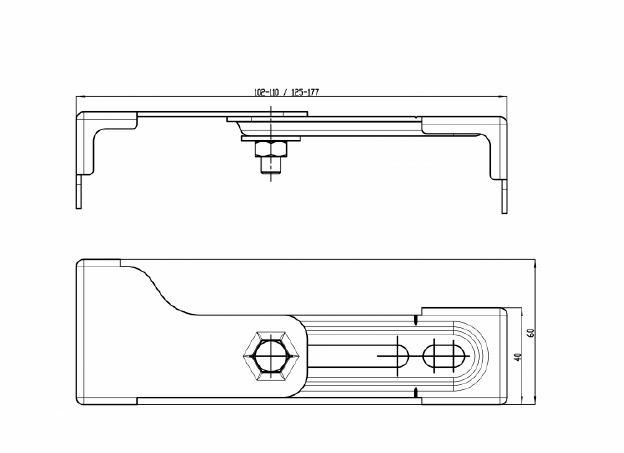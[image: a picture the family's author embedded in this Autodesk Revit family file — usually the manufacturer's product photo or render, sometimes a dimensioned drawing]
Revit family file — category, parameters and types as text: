
# Revit family: PRD_AR_PrplmbInstlFrm_InstallationFrameForUrinal_CMPX136,137
name_source: partatom
category: Plumbing Fixtures
revit_build: Autodesk Revit 2018 (Build: 20190510_1515(x64)
units: mm (PartAtom-declared; Revit-internal decimal feet)

## family parameters
Always vertical = Yes
Cut with Voids When Loaded = Yes
OmniClass Number = 23.40.20.00
OmniClass Title = General Furniture and Specialties
Part Type = Normal
Room Calculation Point = No
Round Connector Dimension = Use Diameter
Shared = Yes
Work Plane-Based = No

## types (2) — shared parameters
1stBeamOffset = 425 mm  [stored 1.39436 ft]
1stBeamOffsetVertical = 425 mm  [stored 1.39436 ft]
2ndBeamOffset = 815 mm  [stored 2.67388 ft]
2ndBeamOffsetVertical = 815 mm  [stored 2.67388 ft]
3rdBeamOffset = 975 mm
4thBeamVisibility = No
AssetType = Fixed
Category = Pr_40_20_93_62, Pre-plumbed installation frames
CisternCapacity = 0
CisternHeight = None
DiameterNominal = 15  [stored 0.0492126 ft]
DurationUnit = year
Features = steel, wall and floor mounting, 525x1120x135 mm (WxHxD)
Finish = powder coated
FlushRate = 0
FlushType = Unset
Form = Installation frame
FrameMaterial = PRD_AR_StainlessSteel_Colored
HeightAdjustment = 200 mm  [stored 0.656168 ft]
IfcExportAs = IfcSanitaryTerminalType
IfcExportType = CISTERN
InletSize = DN 15 (1/2 inch.)
IsAutomaticFlush = 0
IsSingleFlush = 0
Manufacturer = KWC Group AG
ManufacturerName = KWC Group AG
ManufacturerURL = www.kwc.com
Materials = powder coated steel
NBSDescription = Preplumbed installation frames
NBSReference = 45-35-70/421
NominalHeight = 1120 mm  [stored 3.67454 ft]
NominalLength = 135 mm
NominalWidth = 525 mm
OutletOffset = 100 mm  [stored 0.328084 ft]
OutletOffsetVertical = 100 mm  [stored 0.328084 ft]
OutletSize = DN 50 (2 inch.)
OverallHeight = 1120 mm  [stored 3.67454 ft]
PipeMaterial = PRD_AR_OutletPipe
ProductInformation = https://pim.kwc.com
Size = 525x1120x135 mm
SteelMaterial = PRD_AR_StainlessSteel_SatinFinished
URL = www.kwc.com
Uniclass2015Code = Pr_40_20_93_62
Uniclass2015Title = Pre-plumbed installation frames
Uniclass2015Version = Products v1.10
ValveVisibility = No
Version = 1
WarrantyDurationUnit = year
WasteSize = 50  [stored 0.164042 ft]

## per-type parameters (varying)
| type | 2ndBeamVisibility | BIMObjectName | Description | GrossWeight | ModelNumber | Name | NetWeight |
| CMPX136 | Yes | PRD_AR_PreplumbedInstallationFrames_InstallationFrameForUrinal_CMPX136 | AQUAFIX urinal installation frame for stainless steel urinals with siphon control, self-supporting powder coated steel frame construction, MOT-tested, for individual mounting for dry-wall lining, height adjustable fastening of objects, height adjustable fitting connection and outlet mount, premounted for KWC urinal CMPX 538, sound-insulated wall duct G 1/2, universal outlet bend DN 50, urinal fastening bolts, building protection and fixing material. | 9.60 kg | 2030020069 | AQUAFIX urinal installation frame for stainless steel urinals CMPX136 | 9.12 kg |
| CMPX137 | No | PRD_AR_PreplumbedInstallationFrames_InstallationFrameForUrinal_CMPX137 | AQUAFIX urinal installation element for waterfree urinals, self-supporting powder coated steel frame construction, TÜV-tested, for individual mounting for dry-wall lining, height adjustable fastening of objects and outlet mount, premounted for KWC urinal CMPX 538, universal outlet bend DN 50, urinal fastening bolts, building protection, fixing material and mounting instruction. | 9.10 kg | 2030020070 | AQUAFIX urinal installation frame for stainless steel urinals CMPX137 | 8.65 kg |

note: column(s) folded — value = type name in every type: Model, ModelReference

note: [stored X ft] marks values corroborated as IEEE doubles in the binary element streams (Revit-internal decimal feet)

## geometry (parser evidence)
native form markers: Sweep x9
no freeform markers — native parametric forms only
